# Revit family: RN 84227 Optiflex-Flowpress-Valvola combinata
name_source: partatom
category: Rohrzubehör
units: mm (PartAtom-declared; Revit-internal decimal feet)

## family parameters
Arbeitsebenenbasiert = Nein
Beim Laden mit Abzugskörper schneiden = Nein
Bemaßung runder Anschluss = Durchmesser verwenden
Gemeinsam genutzt = Nein
Immer vertikal = Ja
Teiletyp = Ventil - Zerlegung in

## types (2) — shared parameters
1.010.00.2 Blattnummer der Richtlinie = 17
1.010.00.3 Ausgabedatum (Monat) der Richtlinie = 201601
1.010.00.4 Herstellername = R. Nussbaum AG
1.010.00.5 Revisionsdatum der Datei = 20190528
1.010.00.6 Webadresse des Herstellers = http://www.nussbaum.ch
1.100.00.3 Sortiernummer für Anzeigereihenfolge = 1
1.100.00.4 Produktbezeichnung = Absperrarmaturen
1.960/3L.00.8 Link (URL) = https://www.nussbaum.ch
17.700.00.4 Armaturentyp = 1
17.700.00.7 Maximale Betriebstemperatur TB [°C] = 70
17.700.00.8 Maximaler Betriebsdruck (Arbeitsdruck) ps [1.0 · 105 Pa] = 6
CONNECTOR0_dZ_00 = 45 mm
CONNECTOR0_dZ_01 = 31 mm
CONNECTOR0_ref_dY = 31 mm
CONNECTOR0_ref_dZ = 31 mm
CONNECTOR1_DIAMETER_dZ_0r = 12 mm  [stored 0.0393701 ft]
CONNECTOR1_dZ_00 = 33 mm  [stored 0.108268 ft]
CONNECTOR1_dZ_01 = 43 mm
CONNECTOR1_ref_dY = 75 mm
CONNECTOR1_ref_dZ = 33 mm  [stored 0.108268 ft]
Connector Visibility = Nein
EnclosingSpace Visibility = Nein
Hersteller = R. Nussbaum AG
URL = https://www.nussbaum.ch

## per-type parameters (varying)
| type | 1.800.00.3 TGA-Nummer | 1.810.00.3 Hersteller-Bestellnummer | 1.810.00.4 DATANORM-Nummer | 1.810.00.5 StLB-Nummer | 1.810.00.6 GTIN-Nummer | 17.700.00.30 Produktbeschreibung | 17.700.00.5 Nennweite DN | CONNECTOR0_DIAMETER_dZ_0r | Modell | R. Nussbaum AG 84227.21 de Visibility | R. Nussbaum AG 84227.22 de Visibility | Typenkommentare |
| DN 12 | 001102000000000000000000000???0000000000000000000100000000 | 84227.21 | 84227.21 | 322.281 | 7612945735010 | 84227.21, Optiflex-Flowpress-Kombiventil, mit Wandflansch, DN=12 | 12 | 12 mm  [stored 0.0393701 ft] | 84227.21 | Ja | Nein | Optiflex-Flowpress-Valvola combinata DN 12 |
| DN 15 | 001102000000000000000000000???0000000000000000000200000000 | 84227.22 | 84227.22 |  | 7612945735027 | 84227.22, Optiflex-Flowpress-Kombiventil, mit Wandflansch, DN=15 | 15 | 15 mm  [stored 0.0492126 ft] | 84227.22 | Nein | Ja | Optiflex-Flowpress-Valvola combinata DN 15 |

note: [stored X ft] marks values corroborated as IEEE doubles in the binary element streams (Revit-internal decimal feet)

## geometry (parser evidence)
native form markers: Sweep x2
no freeform markers — native parametric forms only
